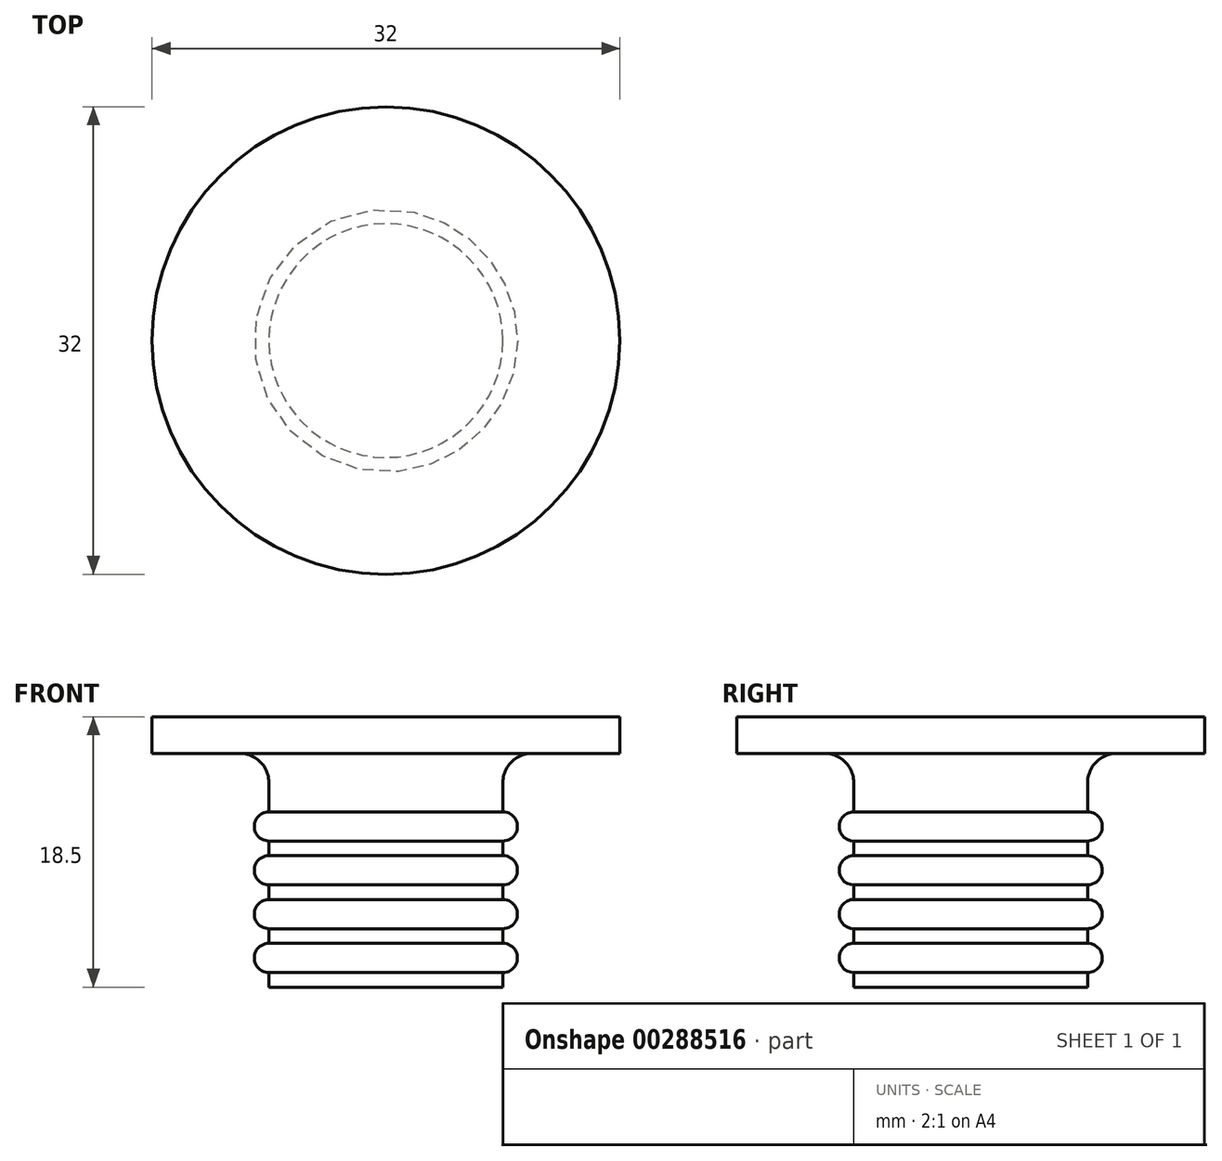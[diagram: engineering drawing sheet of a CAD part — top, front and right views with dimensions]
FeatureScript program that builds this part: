
annotation { "Feature Type Name" : "Feature", "Feature Type Description" : "" }
export const myFeature = defineFeature(function(context is Context, id is Id, definition is map)
    precondition{}
    {
        {
            var Q0;
            Q0=qCreatedBy(makeId("Top.planeOp"),FACE);
            var sketch = newSketch(context, id + "F0", { "sketchPlane" : qUnion([Q0])});
            skCircle(sketch, "E0", {"center": v(0, 0) * mm, "radius": 16 * mm});
            skSolve(sketch);
        }
        {
            var Q0;
            Q0 = qSketchRegion(id + "F0", true);
            extrude(context, id + "F1", {"entities" : qUnion([Q0]), "depth" : 45 * mm});
        }
        {
            var Q0;
            Q0=qCreatedBy(makeId("Front.planeOp"),FACE);
            var sketch = newSketch(context, id + "F2", { "sketchPlane" : qUnion([Q0])});
            skLineSegment(sketch, "E1", {"start": v(-16, 45) * mm, "end": v(16, 21) * mm});
            skLineSegment(sketch, "E2", {"start": v(-16, 45) * mm, "end": v(16, 45) * mm});
            skLineSegment(sketch, "E3", {"start": v(16, 45) * mm, "end": v(16, 21) * mm});
            skSolve(sketch);
        }
        {
            var Q0;
            Q0 = qSketchRegion(id + "F2", true);
            extrude(context, id + "F3", {"entities" : qUnion([Q0]), "operationType" : NewBodyOperationType.REMOVE, "endBound" : BoundingType.SYMMETRIC, "depth" : 50 * mm});
        }
        {
            var Q0;
            Q0=qCreatedBy(makeId("Right.planeOp"),FACE);
            var sketch = newSketch(context, id + "F4", { "sketchPlane" : qUnion([Q0])});
            skLineSegment(sketch, "E4", {"start": v(0, 0) * mm, "end": v(0, 57.36) * mm, "construction": true});
            skLineSegment(sketch, "E5", {"start": v(-20, 16) * mm, "end": v(-10, 16) * mm});
            skLineSegment(sketch, "E6", {"start": v(-8, 0) * mm, "end": v(-20, 0) * mm});
            skLineSegment(sketch, "E7", {"start": v(-20, 0) * mm, "end": v(-20, 16) * mm});
            skLineSegment(sketch, "E8", {"start": v(-9, 15.09) * mm, "end": v(-9, -2.98) * mm, "construction": true});
            skArc(sketch, "E9", {"start": v(-8, 9) * mm, "mid": v(-9, 8) * mm, "end": v(-8, 7) * mm});
            skArc(sketch, "E10", {"start": v(-8, 6) * mm, "mid": v(-9, 5) * mm, "end": v(-8, 4) * mm});
            skArc(sketch, "E11", {"start": v(-8, 3) * mm, "mid": v(-9, 2) * mm, "end": v(-8, 1) * mm});
            skLineSegment(sketch, "E12.trimOffspring", {"start": v(-8, 10) * mm, "end": v(-8, 9) * mm});
            skLineSegment(sketch, "E13.trimOffspring", {"start": v(-8, 7) * mm, "end": v(-8, 6) * mm});
            skLineSegment(sketch, "E14.trimOffspring", {"start": v(-8, 4) * mm, "end": v(-8, 3) * mm});
            skLineSegment(sketch, "E15.trimOffspring", {"start": v(-8, 1) * mm, "end": v(-8, 0) * mm});
            skPoint(sketch, "E16.visualSharp", {"position": v(-8.28, 16) * mm});
            skArc(sketch, "E16.filletArc", {"start": v(-8, 14) * mm, "mid": v(-8.59, 15.41) * mm, "end": v(-10, 16) * mm});
            skArc(sketch, "E17", {"start": v(-8, 12) * mm, "mid": v(-9, 11) * mm, "end": v(-8, 10) * mm});
            skPoint(sketch, "E18.orphan", {"position": v(-8, 10.49) * mm});
            skLineSegment(sketch, "E19", {"start": v(-8, 14) * mm, "end": v(-8, 12) * mm});
            skSolve(sketch);
        }
        {
            var Q0;
            Q0 = qSketchRegion(id + "F4", true);
            var Q1;
            Q1=sQuery(id+"F4.wireOp",EDGE,"E4");
            revolve(context, id + "F5", {"operationType" : NewBodyOperationType.REMOVE, "entities" : qUnion([Q0]), "axis" : qUnion([Q1]), "revolveType" : RevolveType.FULL, "oppositeDirection" : true});
        }
        {
            var Q0;
            Q0=makeQuery(id+"F3.boolean.opBoolean","COPY",FACE,{"derivedFrom":makeQuery(id+"F3.opExtrude","SWEPT_FACE",FACE,{"disambiguationData":[OSD([sQuery(id+"F2.wireOp",EDGE,"E1")])]})});
            var sketch = newSketch(context, id + "F6", { "sketchPlane" : qUnion([Q0])});
            skEllipse(sketch, "E20", {"center": v(-19.3, 0) * mm, "majorRadius": 11.7 * mm, "minorRadius": 19.1 * mm, "majorAxis": v(0, -1)});
            skLineSegment(sketch, "E21", {"start": v(-19.3, -53.76) * mm, "end": v(-19.3, 47.76) * mm, "construction": true});
            skSolve(sketch);
        }
        {
            var Q0;
            Q0 = qSketchRegion(id + "F6", true);
            extrude(context, id + "F7", {"entities" : qUnion([Q0]), "operationType" : NewBodyOperationType.REMOVE, "oppositeDirection" : true, "depth" : 1 * mm});
        }
        {
            var Q0;
            Q0=qCreatedBy(makeId("Front.planeOp"),FACE);
            var sketch = newSketch(context, id + "F8", { "sketchPlane" : qUnion([Q0])});
            skLineSegment(sketch, "E22.bottom", {"start": v(-18.3, 50.5) * mm, "end": v(19.48, 50.5) * mm});
            skLineSegment(sketch, "E22.top", {"start": v(-18.3, 18.5) * mm, "end": v(19.48, 18.5) * mm});
            skLineSegment(sketch, "E22.left", {"start": v(-18.3, 50.5) * mm, "end": v(-18.3, 18.5) * mm});
            skLineSegment(sketch, "E22.right", {"start": v(19.48, 50.5) * mm, "end": v(19.48, 18.5) * mm});
            skSolve(sketch);
        }
        {
            var Q0;
            Q0 = qSketchRegion(id + "F8", true);
            extrude(context, id + "F9", {"entities" : qUnion([Q0]), "operationType" : NewBodyOperationType.REMOVE, "endBound" : BoundingType.SYMMETRIC, "depth" : 50 * mm});
        }
    });
